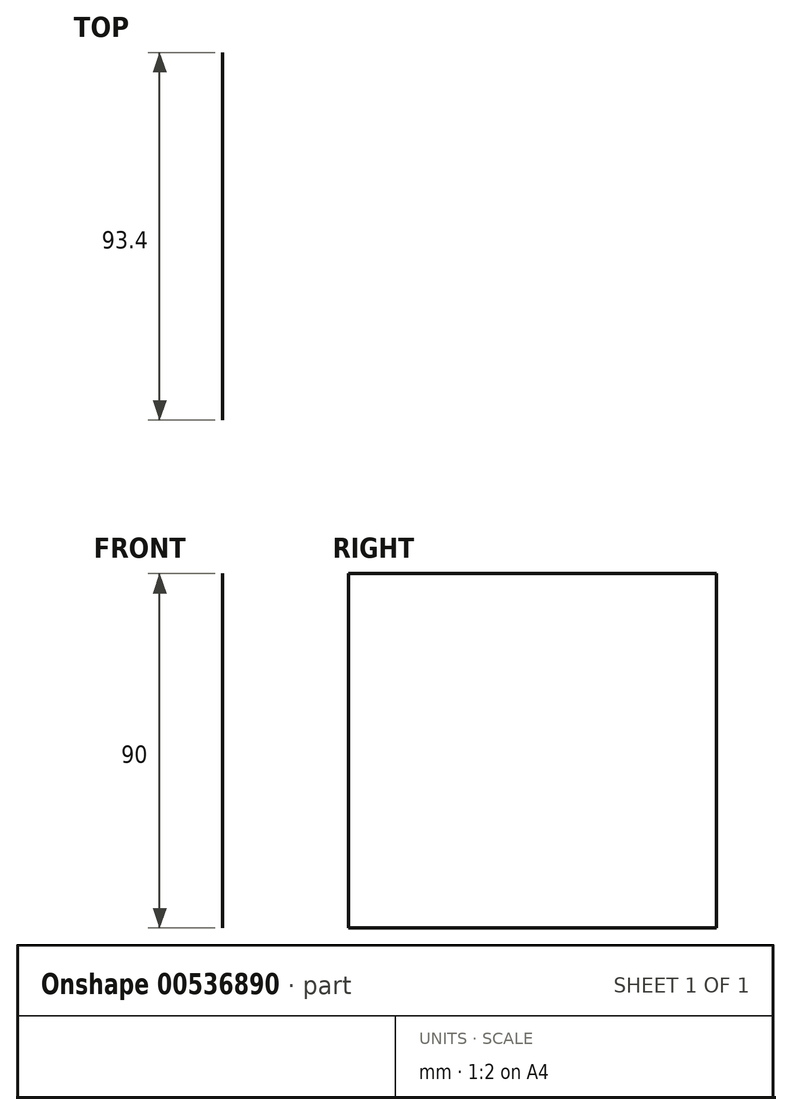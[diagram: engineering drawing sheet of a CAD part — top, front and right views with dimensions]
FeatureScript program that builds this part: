
annotation { "Feature Type Name" : "Feature", "Feature Type Description" : "" }
export const myFeature = defineFeature(function(context is Context, id is Id, definition is map)
    precondition{}
    {
        {
            var Q0;
            Q0=qCreatedBy(makeId("Top.planeOp"),FACE);
            var sketch = newSketch(context, id + "F0", { "sketchPlane" : qUnion([Q0])});
            skLineSegment(sketch, "E0", {"start": v(7.74, -99.3) * mm, "end": v(55.34, -99.3) * mm});
            skLineSegment(sketch, "E1", {"start": v(55.34, -99.3) * mm, "end": v(55.34, 92.52) * mm});
            skLineSegment(sketch, "E2", {"start": v(29.85, -65.8) * mm, "end": v(29.85, 92.52) * mm});
            skLineSegment(sketch, "E3", {"start": v(7.74, -99.3) * mm, "end": v(7.74, 92.52) * mm});
            skLineSegment(sketch, "E4", {"start": v(29.85, 92.52) * mm, "end": v(23.63, 92.52) * mm});
            skLineSegment(sketch, "E5", {"start": v(7.74, 92.52) * mm, "end": v(13.68, 92.52) * mm});
            skLineSegment(sketch, "E6", {"start": v(55.34, 92.52) * mm, "end": v(55.34, 281.08) * mm});
            skLineSegment(sketch, "E7", {"start": v(55.34, 281.08) * mm, "end": v(-184.66, 281.08) * mm});
            skLineSegment(sketch, "E8", {"start": v(-184.66, 281.08) * mm, "end": v(-184.66, 92.52) * mm});
            skLineSegment(sketch, "E9", {"start": v(-184.66, 92.52) * mm, "end": v(7.74, 92.52) * mm});
            skLineSegment(sketch, "E10", {"start": v(-64.66, 92.52) * mm, "end": v(-64.66, 118.77) * mm});
            skLineSegment(sketch, "E11", {"start": v(-64.66, 281.08) * mm, "end": v(-64.66, 187.68) * mm});
            skPoint(sketch, "E11.endSnap0", {"position": v(-64.66, 281.08) * mm});
            skSolve(sketch);
        }
        {
            var Q0;
            Q0=sQuery(id+"F0.wireOp",EDGE,"E11");
            extrude(context, id + "F1", {"bodyType" : ToolBodyType.SURFACE, "surfaceEntities" : qUnion([Q0]), "depth" : 90 * mm, "offsetDistance" : 25 * mm});
        }
    });
